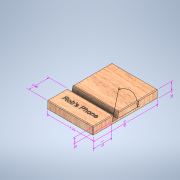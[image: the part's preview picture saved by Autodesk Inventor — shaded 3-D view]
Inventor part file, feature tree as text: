
AUTODESK INVENTOR PART (.ipt)
format: ipt  version: 2021.1 (Build 251245000, 245)  size: 397,312 bytes
history: native  units: in
note: dims shown in document units (in); Inventor stores cm internally (conversion verified against a paired STEP export)
features: other x8, extrude x3, sketch x3, fillet x1
ambient origin geometry x8: Origin, YZ Plane, XZ Plane, XY Plane, X Axis, Y Axis, Z Axis, Center Point
bodies: Solid1 (feature_tree)
feature tree (15):
  other  "Annotations"
  extrude  "Extrusion1"  Depth=6.0in
  extrude  "Extrusion3"  Depth=0.75in
  extrude  "Extrusion4"  TaperAngle=75.0deg  [1 undecoded]
  fillet  "Fillet1"  [1 undecoded]
  sketch  "Sketch2"  dims[d0=4.25in d1=6.0in]
  sketch  "Sketch4"  dims[d2=0.75in d3=0.0in d27=0.5in]
  sketch  "Sketch6"  dims[d28=1.75in d29=75.0deg d31=0.0in d32=0.0in d46=0.5in d50=1.0in d51=0.1in d52=0.0in d53=0.0625in d10=0.0949in d11=4.25in d12=0.3164in d13=0.1734in d14=6.0in d33=0.1905in d34=0.5in d35=0.2828in d36=0.1784in d37=0.75in d41=0.1884in d42=1.75in d43=0.314in d44=0.0802in d45=1.884in d47=0.2389in d48=0.113in d49=75.0deg d9=0.1629in]
  other  "Linear Dimension 1"
  other  "Linear Dimension 2"
  other  "Linear Dimension 3"
  other  "Linear Dimension 4"
  other  "Linear Dimension 5"
  other  "Linear Dimension 6"
  other  "Angular Dimension 1"
note: 2 required parameter values undecoded (feature->parameter linkage not recoverable at this tier; creation-order binding heuristic only, values carry confidence <= 0.55)
